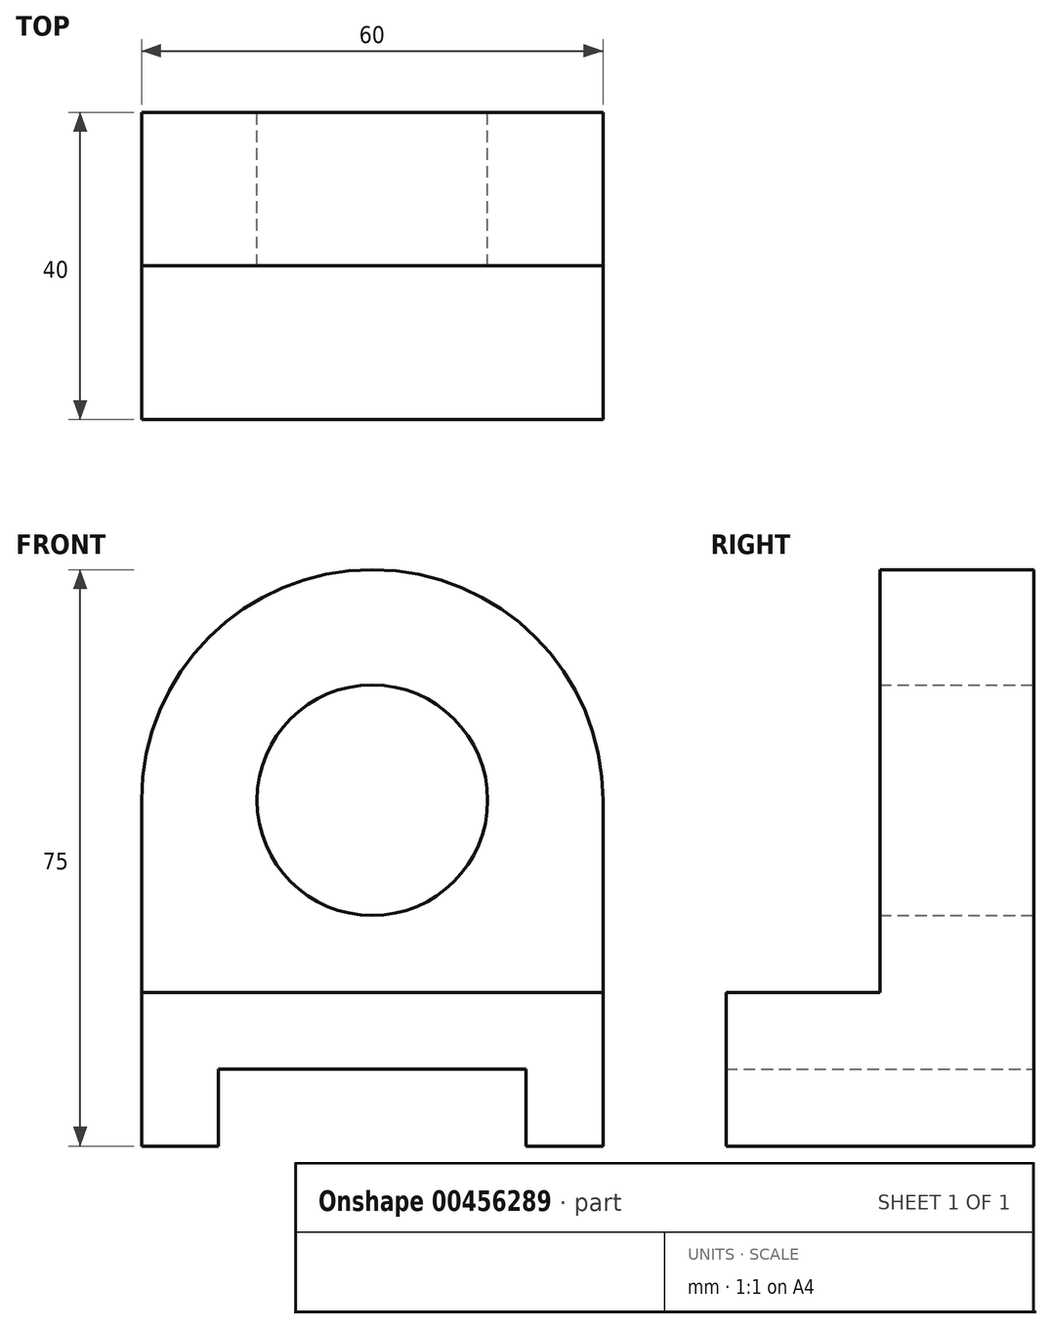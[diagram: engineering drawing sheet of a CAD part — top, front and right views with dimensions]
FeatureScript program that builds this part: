
annotation { "Feature Type Name" : "Feature", "Feature Type Description" : "" }
export const myFeature = defineFeature(function(context is Context, id is Id, definition is map)
    precondition{}
    {
        {
            var Q0;
            Q0=qCreatedBy(makeId("Front.planeOp"),FACE);
            var sketch = newSketch(context, id + "F0", { "sketchPlane" : qUnion([Q0])});
            skLineSegment(sketch, "E0", {"start": v(0, 0) * mm, "end": v(0, 20) * mm});
            skLineSegment(sketch, "E1", {"start": v(0, 20) * mm, "end": v(60, 20) * mm});
            skLineSegment(sketch, "E2", {"start": v(60, 20) * mm, "end": v(60, 0) * mm});
            skLineSegment(sketch, "E3", {"start": v(60, 0) * mm, "end": v(50, 0) * mm});
            skLineSegment(sketch, "E4", {"start": v(50, 0) * mm, "end": v(50, 10) * mm});
            skLineSegment(sketch, "E5", {"start": v(50, 10) * mm, "end": v(10, 10) * mm});
            skLineSegment(sketch, "E6", {"start": v(10, 10) * mm, "end": v(10, 0) * mm});
            skLineSegment(sketch, "E7", {"start": v(10, 0) * mm, "end": v(0, 0) * mm});
            skLineSegment(sketch, "E8", {"start": v(0, 20) * mm, "end": v(0, 45) * mm});
            skLineSegment(sketch, "E9", {"start": v(60, 20) * mm, "end": v(60, 45) * mm});
            skArc(sketch, "E10", {"start": v(60, 45) * mm, "mid": v(30, 75) * mm, "end": v(0, 45) * mm});
            skCircle(sketch, "E11", {"center": v(30, 45) * mm, "radius": 15 * mm});
            skSolve(sketch);
        }
        {
            var Q0;
            Q0=makeQuery(id+"F0.imprint","IMPRINT",FACE,{"disambiguationData":[TD([[makeQuery(id+"F0.imprint","IMPRINT",EDGE,{"derivedFrom":sQuery(id+"F0.wireOp",EDGE,"E0")}),-1.0]])]});
            extrude(context, id + "F1", {"entities" : qUnion([Q0]), "depth" : 40 * mm, "offsetDistance" : 25 * mm});
        }
        {
            var Q0;
            Q0=makeQuery(id+"F0.imprint","IMPRINT",FACE,{"disambiguationData":[TD([[makeQuery(id+"F0.imprint","IMPRINT",EDGE,{"derivedFrom":sQuery(id+"F0.wireOp",EDGE,"E1")}),1.0]])]});
            extrude(context, id + "F2", {"entities" : qUnion([Q0]), "operationType" : NewBodyOperationType.ADD, "depth" : 20 * mm});
        }
    });
